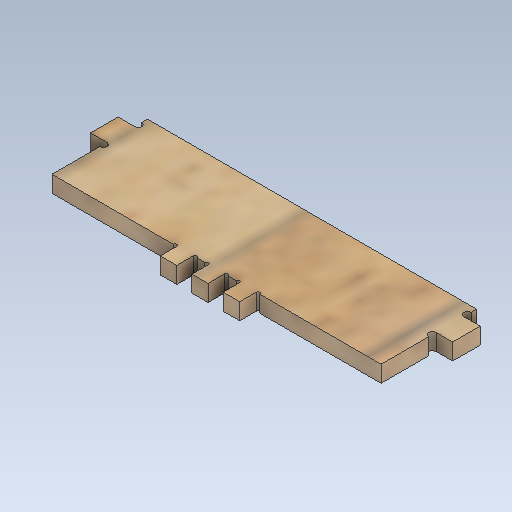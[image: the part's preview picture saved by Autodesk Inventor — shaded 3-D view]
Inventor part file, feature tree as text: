
AUTODESK INVENTOR PART (.ipt)
format: ipt  version: 2020 (Build 240168000, 168)  size: 206,336 bytes
history: native  units: mm
features: extrude x2, sketch x2
ambient origin geometry x8: Origin, YZ Plane, XZ Plane, XY Plane, X Axis, Y Axis, Z Axis, Center Point
bodies: Solid1 (feature_tree)
feature tree (4):
  extrude  "Extrusion1"  Depth=2.666667mm
  extrude  "Extrusion2"  Depth=17.333333mm
  sketch  "Sketch1"  dims[d1=2.0mm d2=2.666667mm]
  sketch  "Sketch2"  dims[d5=2.666667mm d6=17.333333mm d9=6.0mm d10=119.5mm d11=10.0mm d15=1.333333mm d16=1.333333mm d18=44.0mm d19=44.0mm d21=20.0mm d23=6.0mm d24=6.0mm d25=0.0mm d26=6.0mm d27=5.5mm d28=6.0mm d29=6.0mm d30=5.5mm d31=1.333333mm d32=1.333333mm d33=1.333333mm d34=1.333333mm d35=0.0mm d36=0.0mm]
